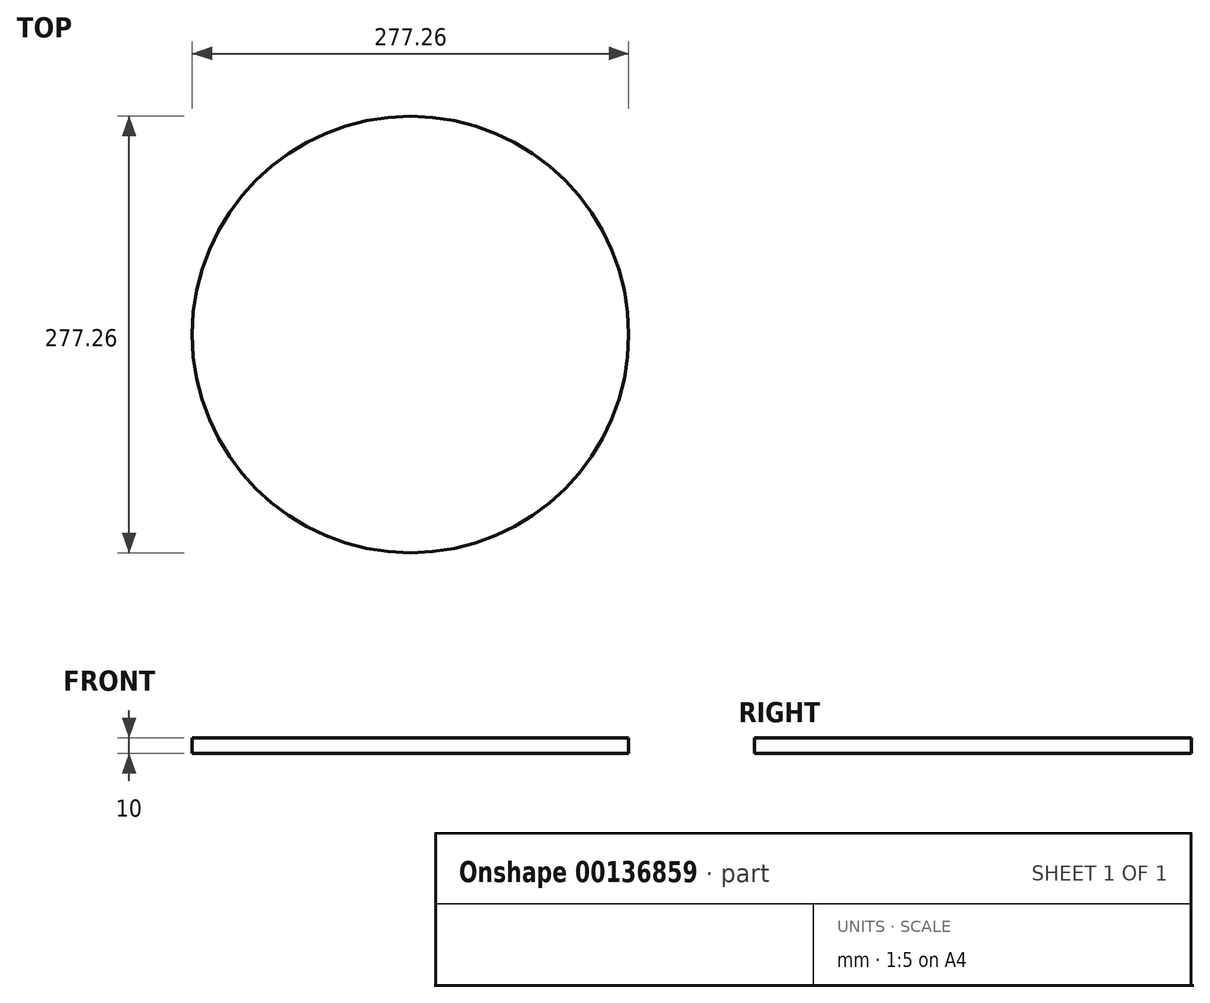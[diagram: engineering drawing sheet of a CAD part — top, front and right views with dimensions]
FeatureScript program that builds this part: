
annotation { "Feature Type Name" : "Feature", "Feature Type Description" : "" }
export const myFeature = defineFeature(function(context is Context, id is Id, definition is map)
    precondition{}
    {
        {
            var Q0;
            Q0=qCreatedBy(makeId("Top.planeOp"),FACE);
            var sketch = newSketch(context, id + "F0", { "sketchPlane" : qUnion([Q0])});
            skCircle(sketch, "E0", {"center": v(0, 0) * mm, "radius": 138.63 * mm});
            skSolve(sketch);
        }
        {
            var Q0;
            Q0 = qSketchRegion(id + "F0", true);
            extrude(context, id + "F1", {"entities" : qUnion([Q0]), "depth" : 10 * mm});
        }
    });
